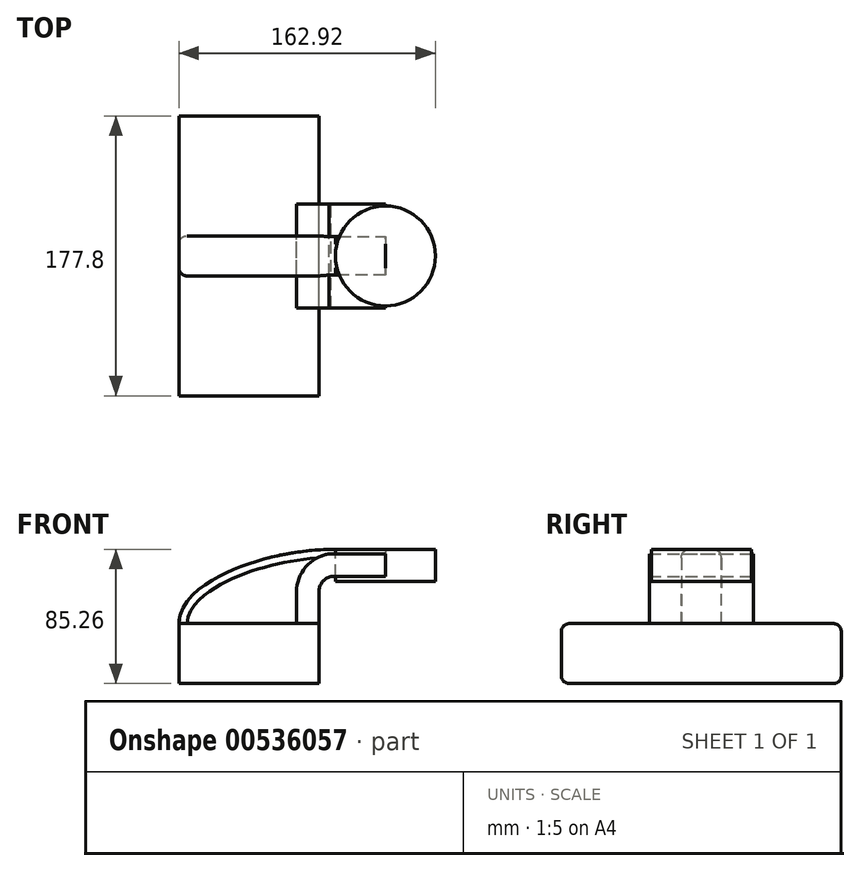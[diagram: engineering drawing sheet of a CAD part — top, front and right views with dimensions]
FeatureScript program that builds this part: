
annotation { "Feature Type Name" : "Feature", "Feature Type Description" : "" }
export const myFeature = defineFeature(function(context is Context, id is Id, definition is map)
    precondition{}
    {
        {
            var Q0;
            Q0=qCreatedBy(makeId("Front.planeOp"),FACE);
            var sketch = newSketch(context, id + "F0", { "sketchPlane" : qUnion([Q0])});
            skLineSegment(sketch, "E0.bottom", {"start": v(44.45, -19.05) * mm, "end": v(-44.45, -19.05) * mm});
            skLineSegment(sketch, "E0.top", {"start": v(44.45, 19.05) * mm, "end": v(-44.45, 19.05) * mm});
            skLineSegment(sketch, "E0.left", {"start": v(44.45, -19.05) * mm, "end": v(44.45, 19.05) * mm});
            skLineSegment(sketch, "E0.right", {"start": v(-44.45, -19.05) * mm, "end": v(-44.45, 19.05) * mm});
            skPoint(sketch, "E0.middle", {"position": v(0, 0) * mm});
            skLineSegment(sketch, "E1.bottom", {"start": v(118.47, 45.88) * mm, "end": v(54.97, 45.88) * mm});
            skLineSegment(sketch, "E1.top", {"start": v(118.47, 66.2) * mm, "end": v(54.97, 66.2) * mm});
            skLineSegment(sketch, "E1.left", {"start": v(118.47, 45.88) * mm, "end": v(118.47, 66.2) * mm});
            skLineSegment(sketch, "E1.right", {"start": v(54.97, 45.88) * mm, "end": v(54.97, 66.2) * mm});
            skPoint(sketch, "E1.middle", {"position": v(86.72, 56.04) * mm});
            skPoint(sketch, "E2.endSnap0", {"position": v(86.72, 45.88) * mm});
            skLineSegment(sketch, "E3", {"start": v(86.72, 66.2) * mm, "end": v(86.72, 45.88) * mm});
            skFitSpline(sketch, "E4", {"points": [v(-44.45, 19.05) * mm, v(54.97, 66.2) * mm], "startDerivative": vector(0.61, 80.89) * mm, "endDerivative": vector(131.81, -0.75) * mm});
            skLineSegment(sketch, "E5", {"start": v(44.45, 19.05) * mm, "end": v(44.45, 39.07) * mm});
            skArc(sketch, "E6", {"start": v(44.45, 39.07) * mm, "mid": v(46.6, 45.38) * mm, "end": v(52.18, 49.05) * mm});
            skLineSegment(sketch, "E7", {"start": v(52.18, 49.05) * mm, "end": v(86.72, 49.05) * mm});
            skLineSegment(sketch, "E8.0", {"start": v(50.75, 63.28) * mm, "end": v(86.72, 63.28) * mm});
            skArc(sketch, "E8.1", {"start": v(30.23, 39.07) * mm, "mid": v(36.05, 54.94) * mm, "end": v(50.75, 63.28) * mm});
            skLineSegment(sketch, "E8.2", {"start": v(30.23, 19.05) * mm, "end": v(30.23, 39.07) * mm});
            skSolve(sketch);
        }
        {
            var Q0;
            Q0=makeQuery(id+"F0.imprint","IMPRINT",FACE,{"disambiguationData":[TD([[makeQuery(id+"F0.imprint","IMPRINT",EDGE,{"derivedFrom":sQuery(id+"F0.wireOp",EDGE,"E0.bottom")}),-1.0]])]});
            extrude(context, id + "F1", {"entities" : qUnion([Q0]), "endBound" : BoundingType.SYMMETRIC, "depth" : 177.8 * mm, "offsetDistance" : 25.4 * mm});
        }
        {
            var Q0;
            {var subQ4=sQuery(id+"F0.wireOp",EDGE,"E1.left");Q0=makeQuery(id+"F0.imprint","IMPRINT",FACE,{"disambiguationData":[TD([[makeQuery(id+"F0.imprint","IMPRINT",EDGE,{"derivedFrom":subQ4}),1.0]])]});}
            var Q1;
            Q1=sQuery(id+"F0.wireOp",EDGE,"E3");
            revolve(context, id + "F2", {"entities" : qUnion([Q0]), "axis" : qUnion([Q1]), "revolveType" : RevolveType.FULL});
        }
        {
            var Q0;
            {var subQ0=sQuery(id+"F0.wireOp",EDGE,"E7");var subQ1=sQuery(id+"F0.wireOp",EDGE,"E1.right");var subQ2=makeQuery(id+"F0.imprint","INTERSECT",VERTEX,{"derivedFrom":[subQ1,subQ0]});Q0=makeQuery(id+"F0.imprint","IMPRINT",FACE,{"disambiguationData":[TD([[makeQuery(id+"F0.imprint","IMPRINT",EDGE,{"disambiguationData":[TD([[subQ2,-1.0]])],"derivedFrom":subQ1}),-1.0]])]});}
            var Q1;
            {var subQ1=sQuery(id+"F0.wireOp",EDGE,"E5");Q1=makeQuery(id+"F0.imprint","IMPRINT",FACE,{"disambiguationData":[TD([[makeQuery(id+"F0.imprint","IMPRINT",EDGE,{"derivedFrom":subQ1}),1.0]])]});}
            extrude(context, id + "F3", {"entities" : qUnion([Q0, Q1]), "endBound" : BoundingType.SYMMETRIC, "depth" : 66.04 * mm, "offsetDistance" : 25.4 * mm});
        }
        {
            var Q0;
            {var subQ4=sQuery(id+"F0.wireOp",EDGE,"E4");Q0=makeQuery(id+"F0.imprint","IMPRINT",FACE,{"disambiguationData":[TD([[makeQuery(id+"F0.imprint","IMPRINT",EDGE,{"derivedFrom":subQ4}),-1.0]])]});}
            var Q1;
            {var subQ1=sQuery(id+"F0.wireOp",EDGE,"E1.top");var subQ3=sQuery(id+"F0.wireOp",EDGE,"E3");var subQ4=makeQuery(id+"F0.imprint","INTERSECT",VERTEX,{"derivedFrom":[subQ1,subQ3]});Q1=makeQuery(id+"F0.imprint","IMPRINT",FACE,{"disambiguationData":[TD([[makeQuery(id+"F0.imprint","IMPRINT",EDGE,{"disambiguationData":[TD([[subQ4,-1.0]])],"derivedFrom":subQ3}),-1.0]])]});}
            extrude(context, id + "F4", {"entities" : qUnion([Q0, Q1]), "endBound" : BoundingType.SYMMETRIC, "depth" : 25.4 * mm, "offsetDistance" : 25.4 * mm});
        }
        {
            var Q0;
            Q0=makeQuery(id+"F1.opExtrude","CAP_EDGE",EDGE,{"disambiguationData":[OSD([sQuery(id+"F0.wireOp",EDGE,"E0.top")])],"isStart":false});
            var Q1;
            Q1=makeQuery(id+"F1.opExtrude","CAP_EDGE",EDGE,{"disambiguationData":[OSD([sQuery(id+"F0.wireOp",EDGE,"E0.bottom")])],"isStart":false});
            var Q2;
            Q2=makeQuery(id+"F1.opExtrude","CAP_EDGE",EDGE,{"disambiguationData":[OSD([sQuery(id+"F0.wireOp",EDGE,"E0.top")])],"isStart":true});
            var Q3;
            Q3=makeQuery(id+"F1.opExtrude","CAP_EDGE",EDGE,{"disambiguationData":[OSD([sQuery(id+"F0.wireOp",EDGE,"E0.bottom")])],"isStart":true});
            var Q4;
            Q4=makeQuery(id+"F4.opExtrude","CAP_EDGE",EDGE,{"disambiguationData":[OSD([sQuery(id+"F0.wireOp",EDGE,"E4")])],"isStart":false});
            var Q5;
            Q5=makeQuery(id+"F4.opExtrude","CAP_EDGE",EDGE,{"disambiguationData":[OSD([sQuery(id+"F0.wireOp",EDGE,"E4")])],"isStart":true});
            fillet(context, id + "F5", {"entities" : qUnion([Q0, Q1, Q2, Q3, Q4, Q5]), "radius" : 5.08 * mm, "tangentPropagation" : true, "allowEdgeOverflow" : false});
        }
    });
